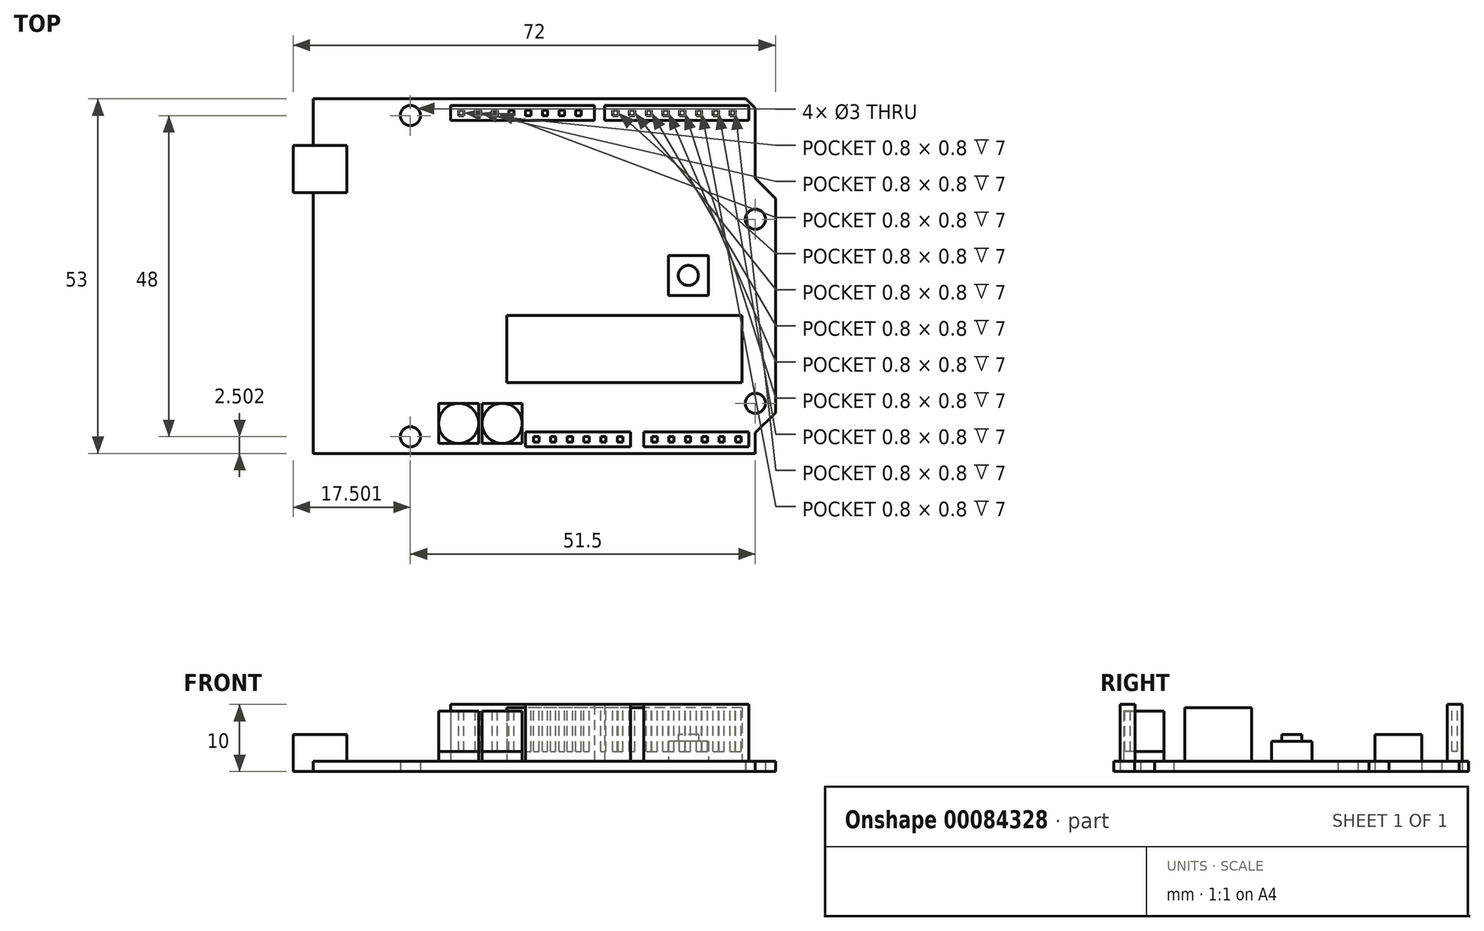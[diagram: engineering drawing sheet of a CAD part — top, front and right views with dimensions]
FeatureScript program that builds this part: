
annotation { "Feature Type Name" : "Feature", "Feature Type Description" : "" }
export const myFeature = defineFeature(function(context is Context, id is Id, definition is map)
    precondition{}
    {
        {
            var Q0;
            Q0=qCreatedBy(makeId("Top.planeOp"),FACE);
            var sketch = newSketch(context, id + "F0", { "sketchPlane" : qUnion([Q0])});
            skLineSegment(sketch, "E0.bottom", {"start": v(-32.88, 24.03) * mm, "end": v(31.7, 24.03) * mm});
            skLineSegment(sketch, "E0.top", {"start": v(-32.88, -28.97) * mm, "end": v(33.12, -28.97) * mm});
            skLineSegment(sketch, "E0.left", {"start": v(-32.88, 24.03) * mm, "end": v(-32.88, -28.97) * mm});
            skLineSegment(sketch, "E0.right", {"start": v(36.12, 9.14) * mm, "end": v(36.12, -22.86) * mm});
            skLineSegment(sketch, "E1", {"start": v(33.12, 22.62) * mm, "end": v(33.12, 12.14) * mm});
            skLineSegment(sketch, "E2", {"start": v(33.12, 12.14) * mm, "end": v(36.12, 9.14) * mm});
            skLineSegment(sketch, "E3", {"start": v(33.12, -25.86) * mm, "end": v(36.12, -22.86) * mm});
            skPoint(sketch, "E4.orphan", {"position": v(36.12, 24.03) * mm});
            skPoint(sketch, "E5.end.orphan", {"position": v(36.12, 11.53) * mm});
            skPoint(sketch, "E6.end.orphan", {"position": v(36.12, -26.47) * mm});
            skPoint(sketch, "E7.orphan", {"position": v(36.12, -28.97) * mm});
            skLineSegment(sketch, "E8.trimOffspring", {"start": v(33.12, -25.86) * mm, "end": v(33.12, -28.97) * mm});
            skCircle(sketch, "E9", {"center": v(33.12, -21.47) * mm, "radius": 1.5 * mm});
            skCircle(sketch, "E10", {"center": v(33.12, 6.03) * mm, "radius": 1.5 * mm});
            skLineSegment(sketch, "E11", {"start": v(31.7, 24.03) * mm, "end": v(33.12, 22.62) * mm});
            skPoint(sketch, "E12.orphan", {"position": v(33.12, 24.03) * mm});
            skCircle(sketch, "E13", {"center": v(-18.38, -26.47) * mm, "radius": 1.5 * mm});
            skCircle(sketch, "E14", {"center": v(-18.38, 21.53) * mm, "radius": 1.5 * mm});
            skLineSegment(sketch, "E15.bottom", {"start": v(-27.88, 17.03) * mm, "end": v(-35.88, 17.03) * mm});
            skLineSegment(sketch, "E15.top", {"start": v(-27.88, 10.03) * mm, "end": v(-35.88, 10.03) * mm});
            skLineSegment(sketch, "E15.left", {"start": v(-27.88, 17.03) * mm, "end": v(-27.88, 10.03) * mm});
            skLineSegment(sketch, "E15.right", {"start": v(-35.88, 17.03) * mm, "end": v(-35.88, 10.03) * mm});
            skSolve(sketch);
        }
        {
            var Q0;
            {var subQ4=sQuery(id+"F0.wireOp",EDGE,"E0.bottom");Q0=makeQuery(id+"F0.imprint","IMPRINT",FACE,{"disambiguationData":[TD([[makeQuery(id+"F0.imprint","IMPRINT",EDGE,{"derivedFrom":subQ4}),-1.0]])]});}
            extrude(context, id + "F1", {"entities" : qUnion([Q0]), "depth" : 1.5 * mm});
        }
        {
            var Q0;
            {var subQ5=sQuery(id+"F0.wireOp",EDGE,"E15.left");Q0=makeQuery(id+"F0.imprint","IMPRINT",FACE,{"disambiguationData":[TD([[makeQuery(id+"F0.imprint","IMPRINT",EDGE,{"derivedFrom":subQ5}),-1.0]])]});}
            var sketch = newSketch(context, id + "F2", { "sketchPlane" : qUnion([Q0])});
            skLineSegment(sketch, "E16.bottom", {"start": v(-27.88, 10.03) * mm, "end": v(-35.88, 10.03) * mm});
            skLineSegment(sketch, "E16.top", {"start": v(-27.88, 17.03) * mm, "end": v(-35.88, 17.03) * mm});
            skLineSegment(sketch, "E16.left", {"start": v(-27.88, 10.03) * mm, "end": v(-27.88, 17.03) * mm});
            skLineSegment(sketch, "E16.right", {"start": v(-35.88, 10.03) * mm, "end": v(-35.88, 17.03) * mm});
            skSolve(sketch);
        }
        {
            var Q0;
            Q0 = qSketchRegion(id + "F2", true);
            extrude(context, id + "F3", {"entities" : qUnion([Q0]), "operationType" : NewBodyOperationType.ADD, "depth" : 5.5 * mm});
        }
        {
            var Q0;
            Q0=makeQuery(id+"F1.opExtrude","CAP_FACE",FACE,{"disambiguationData":[OSD([sQuery(id+"F0.wireOp",EDGE,"E0.bottom"),sQuery(id+"F0.wireOp",EDGE,"E0.top"),sQuery(id+"F0.wireOp",EDGE,"E0.left"),sQuery(id+"F0.wireOp",EDGE,"E0.right"),sQuery(id+"F0.wireOp",EDGE,"E1"),sQuery(id+"F0.wireOp",EDGE,"E2"),sQuery(id+"F0.wireOp",EDGE,"E3"),sQuery(id+"F0.wireOp",EDGE,"E8.trimOffspring"),sQuery(id+"F0.wireOp",EDGE,"E9"),sQuery(id+"F0.wireOp",EDGE,"E10"),sQuery(id+"F0.wireOp",EDGE,"E11"),sQuery(id+"F0.wireOp",EDGE,"E13"),sQuery(id+"F0.wireOp",EDGE,"E14"),sQuery(id+"F0.wireOp",EDGE,"E15.bottom"),sQuery(id+"F0.wireOp",EDGE,"E15.top"),sQuery(id+"F0.wireOp",EDGE,"E15.left")])],"isStart":false});
            var sketch = newSketch(context, id + "F4", { "sketchPlane" : qUnion([Q0])});
            skLineSegment(sketch, "E17.bottom", {"start": v(32.12, 23.03) * mm, "end": v(10.62, 23.03) * mm});
            skLineSegment(sketch, "E17.top", {"start": v(32.12, 20.83) * mm, "end": v(10.62, 20.83) * mm});
            skLineSegment(sketch, "E17.left", {"start": v(32.12, 23.03) * mm, "end": v(32.12, 20.83) * mm});
            skLineSegment(sketch, "E17.right", {"start": v(10.62, 23.03) * mm, "end": v(10.62, 20.83) * mm});
            skLineSegment(sketch, "E18.bottom", {"start": v(9.12, 23.03) * mm, "end": v(-12.38, 23.03) * mm});
            skLineSegment(sketch, "E18.top", {"start": v(9.12, 20.83) * mm, "end": v(-12.38, 20.83) * mm});
            skLineSegment(sketch, "E18.left", {"start": v(9.12, 23.03) * mm, "end": v(9.12, 20.83) * mm});
            skLineSegment(sketch, "E18.right", {"start": v(-12.38, 23.03) * mm, "end": v(-12.38, 20.83) * mm});
            skLineSegment(sketch, "E19.bottom", {"start": v(32.12, -27.97) * mm, "end": v(16.47, -27.97) * mm});
            skLineSegment(sketch, "E19.top", {"start": v(32.12, -25.77) * mm, "end": v(16.47, -25.77) * mm});
            skLineSegment(sketch, "E19.left", {"start": v(32.12, -27.97) * mm, "end": v(32.12, -25.77) * mm});
            skLineSegment(sketch, "E19.right", {"start": v(16.47, -27.97) * mm, "end": v(16.47, -25.77) * mm});
            skLineSegment(sketch, "E20.bottom", {"start": v(14.47, -27.97) * mm, "end": v(-1.18, -27.97) * mm});
            skLineSegment(sketch, "E20.top", {"start": v(14.47, -25.77) * mm, "end": v(-1.18, -25.77) * mm});
            skLineSegment(sketch, "E20.left", {"start": v(14.47, -27.97) * mm, "end": v(14.47, -25.77) * mm});
            skLineSegment(sketch, "E20.right", {"start": v(-1.18, -27.97) * mm, "end": v(-1.18, -25.77) * mm});
            skSolve(sketch);
        }
        {
            var Q0;
            Q0 = qSketchRegion(id + "F4", true);
            extrude(context, id + "F5", {"entities" : qUnion([Q0]), "operationType" : NewBodyOperationType.ADD, "depth" : 8.5 * mm});
        }
        {
            var Q0;
            Q0=makeQuery(id+"F1.opExtrude","CAP_FACE",FACE,{"disambiguationData":[OSD([sQuery(id+"F0.wireOp",EDGE,"E0.bottom"),sQuery(id+"F0.wireOp",EDGE,"E0.top"),sQuery(id+"F0.wireOp",EDGE,"E0.left"),sQuery(id+"F0.wireOp",EDGE,"E0.right"),sQuery(id+"F0.wireOp",EDGE,"E1"),sQuery(id+"F0.wireOp",EDGE,"E2"),sQuery(id+"F0.wireOp",EDGE,"E3"),sQuery(id+"F0.wireOp",EDGE,"E8.trimOffspring"),sQuery(id+"F0.wireOp",EDGE,"E9"),sQuery(id+"F0.wireOp",EDGE,"E10"),sQuery(id+"F0.wireOp",EDGE,"E11"),sQuery(id+"F0.wireOp",EDGE,"E13"),sQuery(id+"F0.wireOp",EDGE,"E14"),sQuery(id+"F0.wireOp",EDGE,"E15.bottom"),sQuery(id+"F0.wireOp",EDGE,"E15.top"),sQuery(id+"F0.wireOp",EDGE,"E15.left")])],"isStart":false});
            var sketch = newSketch(context, id + "F6", { "sketchPlane" : qUnion([Q0])});
            skLineSegment(sketch, "E21.bottom", {"start": v(31.12, -18.37) * mm, "end": v(-3.98, -18.37) * mm});
            skLineSegment(sketch, "E21.top", {"start": v(31.12, -8.37) * mm, "end": v(-3.98, -8.37) * mm});
            skLineSegment(sketch, "E21.left", {"start": v(31.12, -18.37) * mm, "end": v(31.12, -8.37) * mm});
            skLineSegment(sketch, "E21.right", {"start": v(-3.98, -18.37) * mm, "end": v(-3.98, -8.37) * mm});
            skSolve(sketch);
        }
        {
            var Q0;
            Q0 = qSketchRegion(id + "F6", true);
            extrude(context, id + "F7", {"entities" : qUnion([Q0]), "operationType" : NewBodyOperationType.ADD, "depth" : 8 * mm});
        }
        {
            var Q0;
            Q0=makeQuery(id+"F5.opExtrude","CAP_FACE",FACE,{"disambiguationData":[OSD([sQuery(id+"F4.wireOp",EDGE,"E20.bottom"),sQuery(id+"F4.wireOp",EDGE,"E20.top"),sQuery(id+"F4.wireOp",EDGE,"E20.left"),sQuery(id+"F4.wireOp",EDGE,"E20.right")])],"isStart":false});
            var sketch = newSketch(context, id + "F8", { "sketchPlane" : qUnion([Q0])});
            skLineSegment(sketch, "E22.bottom", {"start": v(0.02, -26.47) * mm, "end": v(0.82, -26.47) * mm});
            skLineSegment(sketch, "E22.top", {"start": v(0.02, -27.27) * mm, "end": v(0.82, -27.27) * mm});
            skLineSegment(sketch, "E22.left", {"start": v(0.02, -26.47) * mm, "end": v(0.02, -27.27) * mm});
            skLineSegment(sketch, "E22.right", {"start": v(0.82, -26.47) * mm, "end": v(0.82, -27.27) * mm});
            skLineSegment(sketch, "E23.bottom", {"start": v(-0.48, -25.97) * mm, "end": v(1.32, -25.97) * mm});
            skLineSegment(sketch, "E23.top", {"start": v(-0.48, -27.77) * mm, "end": v(1.32, -27.77) * mm});
            skLineSegment(sketch, "E23.left", {"start": v(-0.48, -25.97) * mm, "end": v(-0.48, -27.77) * mm});
            skLineSegment(sketch, "E23.right", {"start": v(1.32, -25.97) * mm, "end": v(1.32, -27.77) * mm});
            skLineSegment(sketch, "E24.bottom", {"start": v(2.52, -26.47) * mm, "end": v(3.32, -26.47) * mm});
            skLineSegment(sketch, "E24.top", {"start": v(2.52, -27.27) * mm, "end": v(3.32, -27.27) * mm});
            skLineSegment(sketch, "E24.left", {"start": v(2.52, -26.47) * mm, "end": v(2.52, -27.27) * mm});
            skLineSegment(sketch, "E24.right", {"start": v(3.32, -26.47) * mm, "end": v(3.32, -27.27) * mm});
            skLineSegment(sketch, "E25.bottom", {"start": v(2.02, -25.97) * mm, "end": v(3.82, -25.97) * mm});
            skLineSegment(sketch, "E25.top", {"start": v(2.02, -27.77) * mm, "end": v(3.82, -27.77) * mm});
            skLineSegment(sketch, "E25.left", {"start": v(2.02, -25.97) * mm, "end": v(2.02, -27.77) * mm});
            skLineSegment(sketch, "E25.right", {"start": v(3.82, -25.97) * mm, "end": v(3.82, -27.77) * mm});
            skLineSegment(sketch, "E26.bottom", {"start": v(5.02, -26.47) * mm, "end": v(5.82, -26.47) * mm});
            skLineSegment(sketch, "E26.top", {"start": v(5.02, -27.27) * mm, "end": v(5.82, -27.27) * mm});
            skLineSegment(sketch, "E26.left", {"start": v(5.02, -26.47) * mm, "end": v(5.02, -27.27) * mm});
            skLineSegment(sketch, "E26.right", {"start": v(5.82, -26.47) * mm, "end": v(5.82, -27.27) * mm});
            skLineSegment(sketch, "E27.bottom", {"start": v(4.52, -25.97) * mm, "end": v(6.32, -25.97) * mm});
            skLineSegment(sketch, "E27.top", {"start": v(4.52, -27.77) * mm, "end": v(6.32, -27.77) * mm});
            skLineSegment(sketch, "E27.left", {"start": v(4.52, -25.97) * mm, "end": v(4.52, -27.77) * mm});
            skLineSegment(sketch, "E27.right", {"start": v(6.32, -25.97) * mm, "end": v(6.32, -27.77) * mm});
            skLineSegment(sketch, "E28.bottom", {"start": v(7.52, -26.47) * mm, "end": v(8.32, -26.47) * mm});
            skLineSegment(sketch, "E28.top", {"start": v(7.52, -27.27) * mm, "end": v(8.32, -27.27) * mm});
            skLineSegment(sketch, "E28.left", {"start": v(7.52, -26.47) * mm, "end": v(7.52, -27.27) * mm});
            skLineSegment(sketch, "E28.right", {"start": v(8.32, -26.47) * mm, "end": v(8.32, -27.27) * mm});
            skLineSegment(sketch, "E29.bottom", {"start": v(7.02, -25.97) * mm, "end": v(8.82, -25.97) * mm});
            skLineSegment(sketch, "E29.top", {"start": v(7.02, -27.77) * mm, "end": v(8.82, -27.77) * mm});
            skLineSegment(sketch, "E29.left", {"start": v(7.02, -25.97) * mm, "end": v(7.02, -27.77) * mm});
            skLineSegment(sketch, "E29.right", {"start": v(8.82, -25.97) * mm, "end": v(8.82, -27.77) * mm});
            skLineSegment(sketch, "E30.bottom", {"start": v(10.02, -26.47) * mm, "end": v(10.82, -26.47) * mm});
            skLineSegment(sketch, "E30.top", {"start": v(10.02, -27.27) * mm, "end": v(10.82, -27.27) * mm});
            skLineSegment(sketch, "E30.left", {"start": v(10.02, -26.47) * mm, "end": v(10.02, -27.27) * mm});
            skLineSegment(sketch, "E30.right", {"start": v(10.82, -26.47) * mm, "end": v(10.82, -27.27) * mm});
            skLineSegment(sketch, "E31.bottom", {"start": v(9.52, -25.97) * mm, "end": v(11.32, -25.97) * mm});
            skLineSegment(sketch, "E31.top", {"start": v(9.52, -27.77) * mm, "end": v(11.32, -27.77) * mm});
            skLineSegment(sketch, "E31.left", {"start": v(9.52, -25.97) * mm, "end": v(9.52, -27.77) * mm});
            skLineSegment(sketch, "E31.right", {"start": v(11.32, -25.97) * mm, "end": v(11.32, -27.77) * mm});
            skLineSegment(sketch, "E32.bottom", {"start": v(12.52, -26.47) * mm, "end": v(13.32, -26.47) * mm});
            skLineSegment(sketch, "E32.top", {"start": v(12.52, -27.27) * mm, "end": v(13.32, -27.27) * mm});
            skLineSegment(sketch, "E32.left", {"start": v(12.52, -26.47) * mm, "end": v(12.52, -27.27) * mm});
            skLineSegment(sketch, "E32.right", {"start": v(13.32, -26.47) * mm, "end": v(13.32, -27.27) * mm});
            skLineSegment(sketch, "E33.bottom", {"start": v(12.02, -25.97) * mm, "end": v(13.82, -25.97) * mm});
            skLineSegment(sketch, "E33.top", {"start": v(12.02, -27.77) * mm, "end": v(13.82, -27.77) * mm});
            skLineSegment(sketch, "E33.left", {"start": v(12.02, -25.97) * mm, "end": v(12.02, -27.77) * mm});
            skLineSegment(sketch, "E33.right", {"start": v(13.82, -25.97) * mm, "end": v(13.82, -27.77) * mm});
            skLineSegment(sketch, "E34.bottom", {"start": v(17.67, -26.47) * mm, "end": v(18.47, -26.47) * mm});
            skLineSegment(sketch, "E34.top", {"start": v(17.67, -27.27) * mm, "end": v(18.47, -27.27) * mm});
            skLineSegment(sketch, "E34.left", {"start": v(17.67, -26.47) * mm, "end": v(17.67, -27.27) * mm});
            skLineSegment(sketch, "E34.right", {"start": v(18.47, -26.47) * mm, "end": v(18.47, -27.27) * mm});
            skLineSegment(sketch, "E35.bottom", {"start": v(17.17, -25.97) * mm, "end": v(18.97, -25.97) * mm});
            skLineSegment(sketch, "E35.top", {"start": v(17.17, -27.77) * mm, "end": v(18.97, -27.77) * mm});
            skLineSegment(sketch, "E35.left", {"start": v(17.17, -25.97) * mm, "end": v(17.17, -27.77) * mm});
            skLineSegment(sketch, "E35.right", {"start": v(18.97, -25.97) * mm, "end": v(18.97, -27.77) * mm});
            skLineSegment(sketch, "E36.bottom", {"start": v(20.17, -26.47) * mm, "end": v(20.97, -26.47) * mm});
            skLineSegment(sketch, "E36.top", {"start": v(20.17, -27.27) * mm, "end": v(20.97, -27.27) * mm});
            skLineSegment(sketch, "E36.left", {"start": v(20.17, -26.47) * mm, "end": v(20.17, -27.27) * mm});
            skLineSegment(sketch, "E36.right", {"start": v(20.97, -26.47) * mm, "end": v(20.97, -27.27) * mm});
            skLineSegment(sketch, "E37.bottom", {"start": v(19.67, -25.97) * mm, "end": v(21.47, -25.97) * mm});
            skLineSegment(sketch, "E37.top", {"start": v(19.67, -27.77) * mm, "end": v(21.47, -27.77) * mm});
            skLineSegment(sketch, "E37.left", {"start": v(19.67, -25.97) * mm, "end": v(19.67, -27.77) * mm});
            skLineSegment(sketch, "E37.right", {"start": v(21.47, -25.97) * mm, "end": v(21.47, -27.77) * mm});
            skLineSegment(sketch, "E38.bottom", {"start": v(22.67, -26.47) * mm, "end": v(23.47, -26.47) * mm});
            skLineSegment(sketch, "E38.top", {"start": v(22.67, -27.27) * mm, "end": v(23.47, -27.27) * mm});
            skLineSegment(sketch, "E38.left", {"start": v(22.67, -26.47) * mm, "end": v(22.67, -27.27) * mm});
            skLineSegment(sketch, "E38.right", {"start": v(23.47, -26.47) * mm, "end": v(23.47, -27.27) * mm});
            skLineSegment(sketch, "E39.bottom", {"start": v(22.17, -25.97) * mm, "end": v(23.97, -25.97) * mm});
            skLineSegment(sketch, "E39.top", {"start": v(22.17, -27.77) * mm, "end": v(23.97, -27.77) * mm});
            skLineSegment(sketch, "E39.left", {"start": v(22.17, -25.97) * mm, "end": v(22.17, -27.77) * mm});
            skLineSegment(sketch, "E39.right", {"start": v(23.97, -25.97) * mm, "end": v(23.97, -27.77) * mm});
            skLineSegment(sketch, "E40.bottom", {"start": v(25.17, -26.47) * mm, "end": v(25.97, -26.47) * mm});
            skLineSegment(sketch, "E40.top", {"start": v(25.17, -27.27) * mm, "end": v(25.97, -27.27) * mm});
            skLineSegment(sketch, "E40.left", {"start": v(25.17, -26.47) * mm, "end": v(25.17, -27.27) * mm});
            skLineSegment(sketch, "E40.right", {"start": v(25.97, -26.47) * mm, "end": v(25.97, -27.27) * mm});
            skLineSegment(sketch, "E41.bottom", {"start": v(24.67, -25.97) * mm, "end": v(26.47, -25.97) * mm});
            skLineSegment(sketch, "E41.top", {"start": v(24.67, -27.77) * mm, "end": v(26.47, -27.77) * mm});
            skLineSegment(sketch, "E41.left", {"start": v(24.67, -25.97) * mm, "end": v(24.67, -27.77) * mm});
            skLineSegment(sketch, "E41.right", {"start": v(26.47, -25.97) * mm, "end": v(26.47, -27.77) * mm});
            skLineSegment(sketch, "E42.bottom", {"start": v(27.67, -26.47) * mm, "end": v(28.47, -26.47) * mm});
            skLineSegment(sketch, "E42.top", {"start": v(27.67, -27.27) * mm, "end": v(28.47, -27.27) * mm});
            skLineSegment(sketch, "E42.left", {"start": v(27.67, -26.47) * mm, "end": v(27.67, -27.27) * mm});
            skLineSegment(sketch, "E42.right", {"start": v(28.47, -26.47) * mm, "end": v(28.47, -27.27) * mm});
            skLineSegment(sketch, "E43.bottom", {"start": v(27.17, -25.97) * mm, "end": v(28.97, -25.97) * mm});
            skLineSegment(sketch, "E43.top", {"start": v(27.17, -27.77) * mm, "end": v(28.97, -27.77) * mm});
            skLineSegment(sketch, "E43.left", {"start": v(27.17, -25.97) * mm, "end": v(27.17, -27.77) * mm});
            skLineSegment(sketch, "E43.right", {"start": v(28.97, -25.97) * mm, "end": v(28.97, -27.77) * mm});
            skLineSegment(sketch, "E44.bottom", {"start": v(30.17, -26.47) * mm, "end": v(30.97, -26.47) * mm});
            skLineSegment(sketch, "E44.top", {"start": v(30.17, -27.27) * mm, "end": v(30.97, -27.27) * mm});
            skLineSegment(sketch, "E44.left", {"start": v(30.17, -26.47) * mm, "end": v(30.17, -27.27) * mm});
            skLineSegment(sketch, "E44.right", {"start": v(30.97, -26.47) * mm, "end": v(30.97, -27.27) * mm});
            skLineSegment(sketch, "E45.bottom", {"start": v(29.67, -25.97) * mm, "end": v(31.47, -25.97) * mm});
            skLineSegment(sketch, "E45.top", {"start": v(29.67, -27.77) * mm, "end": v(31.47, -27.77) * mm});
            skLineSegment(sketch, "E45.left", {"start": v(29.67, -25.97) * mm, "end": v(29.67, -27.77) * mm});
            skLineSegment(sketch, "E45.right", {"start": v(31.47, -25.97) * mm, "end": v(31.47, -27.77) * mm});
            skLineSegment(sketch, "E46.bottom", {"start": v(-11.18, 22.33) * mm, "end": v(-10.38, 22.33) * mm});
            skLineSegment(sketch, "E46.top", {"start": v(-11.18, 21.53) * mm, "end": v(-10.38, 21.53) * mm});
            skLineSegment(sketch, "E46.left", {"start": v(-11.18, 22.33) * mm, "end": v(-11.18, 21.53) * mm});
            skLineSegment(sketch, "E46.right", {"start": v(-10.38, 22.33) * mm, "end": v(-10.38, 21.53) * mm});
            skLineSegment(sketch, "E47.bottom", {"start": v(-11.68, 22.83) * mm, "end": v(-9.88, 22.83) * mm});
            skLineSegment(sketch, "E47.top", {"start": v(-11.68, 21.03) * mm, "end": v(-9.88, 21.03) * mm});
            skLineSegment(sketch, "E47.left", {"start": v(-11.68, 22.83) * mm, "end": v(-11.68, 21.03) * mm});
            skLineSegment(sketch, "E47.right", {"start": v(-9.88, 22.83) * mm, "end": v(-9.88, 21.03) * mm});
            skLineSegment(sketch, "E48.bottom", {"start": v(-8.68, 22.33) * mm, "end": v(-7.88, 22.33) * mm});
            skLineSegment(sketch, "E48.top", {"start": v(-8.68, 21.53) * mm, "end": v(-7.88, 21.53) * mm});
            skLineSegment(sketch, "E48.left", {"start": v(-8.68, 22.33) * mm, "end": v(-8.68, 21.53) * mm});
            skLineSegment(sketch, "E48.right", {"start": v(-7.88, 22.33) * mm, "end": v(-7.88, 21.53) * mm});
            skLineSegment(sketch, "E49.bottom", {"start": v(-9.18, 22.83) * mm, "end": v(-7.38, 22.83) * mm});
            skLineSegment(sketch, "E49.top", {"start": v(-9.18, 21.03) * mm, "end": v(-7.38, 21.03) * mm});
            skLineSegment(sketch, "E49.left", {"start": v(-9.18, 22.83) * mm, "end": v(-9.18, 21.03) * mm});
            skLineSegment(sketch, "E49.right", {"start": v(-7.38, 22.83) * mm, "end": v(-7.38, 21.03) * mm});
            skLineSegment(sketch, "E50.bottom", {"start": v(-6.18, 22.33) * mm, "end": v(-5.38, 22.33) * mm});
            skLineSegment(sketch, "E50.top", {"start": v(-6.18, 21.53) * mm, "end": v(-5.38, 21.53) * mm});
            skLineSegment(sketch, "E50.left", {"start": v(-6.18, 22.33) * mm, "end": v(-6.18, 21.53) * mm});
            skLineSegment(sketch, "E50.right", {"start": v(-5.38, 22.33) * mm, "end": v(-5.38, 21.53) * mm});
            skLineSegment(sketch, "E51.bottom", {"start": v(-6.68, 22.83) * mm, "end": v(-4.88, 22.83) * mm});
            skLineSegment(sketch, "E51.top", {"start": v(-6.68, 21.03) * mm, "end": v(-4.88, 21.03) * mm});
            skLineSegment(sketch, "E51.left", {"start": v(-6.68, 22.83) * mm, "end": v(-6.68, 21.03) * mm});
            skLineSegment(sketch, "E51.right", {"start": v(-4.88, 22.83) * mm, "end": v(-4.88, 21.03) * mm});
            skLineSegment(sketch, "E52.bottom", {"start": v(-3.68, 22.33) * mm, "end": v(-2.88, 22.33) * mm});
            skLineSegment(sketch, "E52.top", {"start": v(-3.68, 21.53) * mm, "end": v(-2.88, 21.53) * mm});
            skLineSegment(sketch, "E52.left", {"start": v(-3.68, 22.33) * mm, "end": v(-3.68, 21.53) * mm});
            skLineSegment(sketch, "E52.right", {"start": v(-2.88, 22.33) * mm, "end": v(-2.88, 21.53) * mm});
            skLineSegment(sketch, "E53.bottom", {"start": v(-4.18, 22.83) * mm, "end": v(-2.38, 22.83) * mm});
            skLineSegment(sketch, "E53.top", {"start": v(-4.18, 21.03) * mm, "end": v(-2.38, 21.03) * mm});
            skLineSegment(sketch, "E53.left", {"start": v(-4.18, 22.83) * mm, "end": v(-4.18, 21.03) * mm});
            skLineSegment(sketch, "E53.right", {"start": v(-2.38, 22.83) * mm, "end": v(-2.38, 21.03) * mm});
            skLineSegment(sketch, "E54.bottom", {"start": v(-1.18, 22.33) * mm, "end": v(-0.38, 22.33) * mm});
            skLineSegment(sketch, "E54.top", {"start": v(-1.18, 21.53) * mm, "end": v(-0.38, 21.53) * mm});
            skLineSegment(sketch, "E54.left", {"start": v(-1.18, 22.33) * mm, "end": v(-1.18, 21.53) * mm});
            skLineSegment(sketch, "E54.right", {"start": v(-0.38, 22.33) * mm, "end": v(-0.38, 21.53) * mm});
            skLineSegment(sketch, "E55.bottom", {"start": v(-1.68, 22.83) * mm, "end": v(0.12, 22.83) * mm});
            skLineSegment(sketch, "E55.top", {"start": v(-1.68, 21.03) * mm, "end": v(0.12, 21.03) * mm});
            skLineSegment(sketch, "E55.left", {"start": v(-1.68, 22.83) * mm, "end": v(-1.68, 21.03) * mm});
            skLineSegment(sketch, "E55.right", {"start": v(0.12, 22.83) * mm, "end": v(0.12, 21.03) * mm});
            skLineSegment(sketch, "E56.bottom", {"start": v(1.32, 22.33) * mm, "end": v(2.12, 22.33) * mm});
            skLineSegment(sketch, "E56.top", {"start": v(1.32, 21.53) * mm, "end": v(2.12, 21.53) * mm});
            skLineSegment(sketch, "E56.left", {"start": v(1.32, 22.33) * mm, "end": v(1.32, 21.53) * mm});
            skLineSegment(sketch, "E56.right", {"start": v(2.12, 22.33) * mm, "end": v(2.12, 21.53) * mm});
            skLineSegment(sketch, "E57.bottom", {"start": v(0.82, 22.83) * mm, "end": v(2.62, 22.83) * mm});
            skLineSegment(sketch, "E57.top", {"start": v(0.82, 21.03) * mm, "end": v(2.62, 21.03) * mm});
            skLineSegment(sketch, "E57.left", {"start": v(0.82, 22.83) * mm, "end": v(0.82, 21.03) * mm});
            skLineSegment(sketch, "E57.right", {"start": v(2.62, 22.83) * mm, "end": v(2.62, 21.03) * mm});
            skLineSegment(sketch, "E58.bottom", {"start": v(3.82, 22.33) * mm, "end": v(4.62, 22.33) * mm});
            skLineSegment(sketch, "E58.top", {"start": v(3.82, 21.53) * mm, "end": v(4.62, 21.53) * mm});
            skLineSegment(sketch, "E58.left", {"start": v(3.82, 22.33) * mm, "end": v(3.82, 21.53) * mm});
            skLineSegment(sketch, "E58.right", {"start": v(4.62, 22.33) * mm, "end": v(4.62, 21.53) * mm});
            skLineSegment(sketch, "E59.bottom", {"start": v(3.32, 22.83) * mm, "end": v(5.12, 22.83) * mm});
            skLineSegment(sketch, "E59.top", {"start": v(3.32, 21.03) * mm, "end": v(5.12, 21.03) * mm});
            skLineSegment(sketch, "E59.left", {"start": v(3.32, 22.83) * mm, "end": v(3.32, 21.03) * mm});
            skLineSegment(sketch, "E59.right", {"start": v(5.12, 22.83) * mm, "end": v(5.12, 21.03) * mm});
            skLineSegment(sketch, "E60.bottom", {"start": v(6.32, 22.33) * mm, "end": v(7.12, 22.33) * mm});
            skLineSegment(sketch, "E60.top", {"start": v(6.32, 21.53) * mm, "end": v(7.12, 21.53) * mm});
            skLineSegment(sketch, "E60.left", {"start": v(6.32, 22.33) * mm, "end": v(6.32, 21.53) * mm});
            skLineSegment(sketch, "E60.right", {"start": v(7.12, 22.33) * mm, "end": v(7.12, 21.53) * mm});
            skLineSegment(sketch, "E61.bottom", {"start": v(5.82, 22.83) * mm, "end": v(7.62, 22.83) * mm});
            skLineSegment(sketch, "E61.top", {"start": v(5.82, 21.03) * mm, "end": v(7.62, 21.03) * mm});
            skLineSegment(sketch, "E61.left", {"start": v(5.82, 22.83) * mm, "end": v(5.82, 21.03) * mm});
            skLineSegment(sketch, "E61.right", {"start": v(7.62, 22.83) * mm, "end": v(7.62, 21.03) * mm});
            skLineSegment(sketch, "E62.bottom", {"start": v(11.82, 22.33) * mm, "end": v(12.62, 22.33) * mm});
            skLineSegment(sketch, "E62.top", {"start": v(11.82, 21.53) * mm, "end": v(12.62, 21.53) * mm});
            skLineSegment(sketch, "E62.left", {"start": v(11.82, 22.33) * mm, "end": v(11.82, 21.53) * mm});
            skLineSegment(sketch, "E62.right", {"start": v(12.62, 22.33) * mm, "end": v(12.62, 21.53) * mm});
            skLineSegment(sketch, "E63.bottom", {"start": v(11.32, 22.83) * mm, "end": v(13.12, 22.83) * mm});
            skLineSegment(sketch, "E63.top", {"start": v(11.32, 21.03) * mm, "end": v(13.12, 21.03) * mm});
            skLineSegment(sketch, "E63.left", {"start": v(11.32, 22.83) * mm, "end": v(11.32, 21.03) * mm});
            skLineSegment(sketch, "E63.right", {"start": v(13.12, 22.83) * mm, "end": v(13.12, 21.03) * mm});
            skLineSegment(sketch, "E64.bottom", {"start": v(14.32, 22.33) * mm, "end": v(15.12, 22.33) * mm});
            skLineSegment(sketch, "E64.top", {"start": v(14.32, 21.53) * mm, "end": v(15.12, 21.53) * mm});
            skLineSegment(sketch, "E64.left", {"start": v(14.32, 22.33) * mm, "end": v(14.32, 21.53) * mm});
            skLineSegment(sketch, "E64.right", {"start": v(15.12, 22.33) * mm, "end": v(15.12, 21.53) * mm});
            skLineSegment(sketch, "E65.bottom", {"start": v(13.82, 22.83) * mm, "end": v(15.62, 22.83) * mm});
            skLineSegment(sketch, "E65.top", {"start": v(13.82, 21.03) * mm, "end": v(15.62, 21.03) * mm});
            skLineSegment(sketch, "E65.left", {"start": v(13.82, 22.83) * mm, "end": v(13.82, 21.03) * mm});
            skLineSegment(sketch, "E65.right", {"start": v(15.62, 22.83) * mm, "end": v(15.62, 21.03) * mm});
            skLineSegment(sketch, "E66.bottom", {"start": v(16.82, 22.33) * mm, "end": v(17.62, 22.33) * mm});
            skLineSegment(sketch, "E66.top", {"start": v(16.82, 21.53) * mm, "end": v(17.62, 21.53) * mm});
            skLineSegment(sketch, "E66.left", {"start": v(16.82, 22.33) * mm, "end": v(16.82, 21.53) * mm});
            skLineSegment(sketch, "E66.right", {"start": v(17.62, 22.33) * mm, "end": v(17.62, 21.53) * mm});
            skLineSegment(sketch, "E67.bottom", {"start": v(16.32, 22.83) * mm, "end": v(18.12, 22.83) * mm});
            skLineSegment(sketch, "E67.top", {"start": v(16.32, 21.03) * mm, "end": v(18.12, 21.03) * mm});
            skLineSegment(sketch, "E67.left", {"start": v(16.32, 22.83) * mm, "end": v(16.32, 21.03) * mm});
            skLineSegment(sketch, "E67.right", {"start": v(18.12, 22.83) * mm, "end": v(18.12, 21.03) * mm});
            skLineSegment(sketch, "E68.bottom", {"start": v(19.32, 22.33) * mm, "end": v(20.12, 22.33) * mm});
            skLineSegment(sketch, "E68.top", {"start": v(19.32, 21.53) * mm, "end": v(20.12, 21.53) * mm});
            skLineSegment(sketch, "E68.left", {"start": v(19.32, 22.33) * mm, "end": v(19.32, 21.53) * mm});
            skLineSegment(sketch, "E68.right", {"start": v(20.12, 22.33) * mm, "end": v(20.12, 21.53) * mm});
            skLineSegment(sketch, "E69.bottom", {"start": v(18.82, 22.83) * mm, "end": v(20.62, 22.83) * mm});
            skLineSegment(sketch, "E69.top", {"start": v(18.82, 21.03) * mm, "end": v(20.62, 21.03) * mm});
            skLineSegment(sketch, "E69.left", {"start": v(18.82, 22.83) * mm, "end": v(18.82, 21.03) * mm});
            skLineSegment(sketch, "E69.right", {"start": v(20.62, 22.83) * mm, "end": v(20.62, 21.03) * mm});
            skLineSegment(sketch, "E70.bottom", {"start": v(21.82, 22.33) * mm, "end": v(22.62, 22.33) * mm});
            skLineSegment(sketch, "E70.top", {"start": v(21.82, 21.53) * mm, "end": v(22.62, 21.53) * mm});
            skLineSegment(sketch, "E70.left", {"start": v(21.82, 22.33) * mm, "end": v(21.82, 21.53) * mm});
            skLineSegment(sketch, "E70.right", {"start": v(22.62, 22.33) * mm, "end": v(22.62, 21.53) * mm});
            skLineSegment(sketch, "E71.bottom", {"start": v(21.32, 22.83) * mm, "end": v(23.12, 22.83) * mm});
            skLineSegment(sketch, "E71.top", {"start": v(21.32, 21.03) * mm, "end": v(23.12, 21.03) * mm});
            skLineSegment(sketch, "E71.left", {"start": v(21.32, 22.83) * mm, "end": v(21.32, 21.03) * mm});
            skLineSegment(sketch, "E71.right", {"start": v(23.12, 22.83) * mm, "end": v(23.12, 21.03) * mm});
            skLineSegment(sketch, "E72.bottom", {"start": v(24.32, 22.33) * mm, "end": v(25.12, 22.33) * mm});
            skLineSegment(sketch, "E72.top", {"start": v(24.32, 21.53) * mm, "end": v(25.12, 21.53) * mm});
            skLineSegment(sketch, "E72.left", {"start": v(24.32, 22.33) * mm, "end": v(24.32, 21.53) * mm});
            skLineSegment(sketch, "E72.right", {"start": v(25.12, 22.33) * mm, "end": v(25.12, 21.53) * mm});
            skLineSegment(sketch, "E73.bottom", {"start": v(23.82, 22.83) * mm, "end": v(25.62, 22.83) * mm});
            skLineSegment(sketch, "E73.top", {"start": v(23.82, 21.03) * mm, "end": v(25.62, 21.03) * mm});
            skLineSegment(sketch, "E73.left", {"start": v(23.82, 22.83) * mm, "end": v(23.82, 21.03) * mm});
            skLineSegment(sketch, "E73.right", {"start": v(25.62, 22.83) * mm, "end": v(25.62, 21.03) * mm});
            skLineSegment(sketch, "E74.bottom", {"start": v(26.82, 22.33) * mm, "end": v(27.62, 22.33) * mm});
            skLineSegment(sketch, "E74.top", {"start": v(26.82, 21.53) * mm, "end": v(27.62, 21.53) * mm});
            skLineSegment(sketch, "E74.left", {"start": v(26.82, 22.33) * mm, "end": v(26.82, 21.53) * mm});
            skLineSegment(sketch, "E74.right", {"start": v(27.62, 22.33) * mm, "end": v(27.62, 21.53) * mm});
            skLineSegment(sketch, "E75.bottom", {"start": v(26.32, 22.83) * mm, "end": v(28.12, 22.83) * mm});
            skLineSegment(sketch, "E75.top", {"start": v(26.32, 21.03) * mm, "end": v(28.12, 21.03) * mm});
            skLineSegment(sketch, "E75.left", {"start": v(26.32, 22.83) * mm, "end": v(26.32, 21.03) * mm});
            skLineSegment(sketch, "E75.right", {"start": v(28.12, 22.83) * mm, "end": v(28.12, 21.03) * mm});
            skLineSegment(sketch, "E76.bottom", {"start": v(29.32, 22.33) * mm, "end": v(30.12, 22.33) * mm});
            skLineSegment(sketch, "E76.top", {"start": v(29.32, 21.53) * mm, "end": v(30.12, 21.53) * mm});
            skLineSegment(sketch, "E76.left", {"start": v(29.32, 22.33) * mm, "end": v(29.32, 21.53) * mm});
            skLineSegment(sketch, "E76.right", {"start": v(30.12, 22.33) * mm, "end": v(30.12, 21.53) * mm});
            skLineSegment(sketch, "E77.bottom", {"start": v(28.82, 22.83) * mm, "end": v(30.62, 22.83) * mm});
            skLineSegment(sketch, "E77.top", {"start": v(28.82, 21.03) * mm, "end": v(30.62, 21.03) * mm});
            skLineSegment(sketch, "E77.left", {"start": v(28.82, 22.83) * mm, "end": v(28.82, 21.03) * mm});
            skLineSegment(sketch, "E77.right", {"start": v(30.62, 22.83) * mm, "end": v(30.62, 21.03) * mm});
            skSolve(sketch);
        }
        {
            var Q0;
            Q0=makeQuery(id+"F8.imprint","IMPRINT",FACE,{"disambiguationData":[TD([[makeQuery(id+"F8.imprint","IMPRINT",EDGE,{"derivedFrom":sQuery(id+"F8.wireOp",EDGE,"E60.bottom")}),-1.0]])]});
            var Q1;
            Q1=makeQuery(id+"F8.imprint","IMPRINT",FACE,{"disambiguationData":[TD([[makeQuery(id+"F8.imprint","IMPRINT",EDGE,{"derivedFrom":sQuery(id+"F8.wireOp",EDGE,"E58.bottom")}),-1.0]])]});
            var Q2;
            Q2=makeQuery(id+"F8.imprint","IMPRINT",FACE,{"disambiguationData":[TD([[makeQuery(id+"F8.imprint","IMPRINT",EDGE,{"derivedFrom":sQuery(id+"F8.wireOp",EDGE,"E62.bottom")}),-1.0]])]});
            var Q3;
            Q3=makeQuery(id+"F8.imprint","IMPRINT",FACE,{"disambiguationData":[TD([[makeQuery(id+"F8.imprint","IMPRINT",EDGE,{"derivedFrom":sQuery(id+"F8.wireOp",EDGE,"E64.bottom")}),-1.0]])]});
            var Q4;
            Q4=makeQuery(id+"F8.imprint","IMPRINT",FACE,{"disambiguationData":[TD([[makeQuery(id+"F8.imprint","IMPRINT",EDGE,{"derivedFrom":sQuery(id+"F8.wireOp",EDGE,"E66.bottom")}),-1.0]])]});
            var Q5;
            Q5=makeQuery(id+"F8.imprint","IMPRINT",FACE,{"disambiguationData":[TD([[makeQuery(id+"F8.imprint","IMPRINT",EDGE,{"derivedFrom":sQuery(id+"F8.wireOp",EDGE,"E68.bottom")}),-1.0]])]});
            var Q6;
            Q6=makeQuery(id+"F8.imprint","IMPRINT",FACE,{"disambiguationData":[TD([[makeQuery(id+"F8.imprint","IMPRINT",EDGE,{"derivedFrom":sQuery(id+"F8.wireOp",EDGE,"E70.bottom")}),-1.0]])]});
            var Q7;
            Q7=makeQuery(id+"F8.imprint","IMPRINT",FACE,{"disambiguationData":[TD([[makeQuery(id+"F8.imprint","IMPRINT",EDGE,{"derivedFrom":sQuery(id+"F8.wireOp",EDGE,"E74.bottom")}),-1.0]])]});
            var Q8;
            Q8=makeQuery(id+"F8.imprint","IMPRINT",FACE,{"disambiguationData":[TD([[makeQuery(id+"F8.imprint","IMPRINT",EDGE,{"derivedFrom":sQuery(id+"F8.wireOp",EDGE,"E76.bottom")}),-1.0]])]});
            var Q9;
            Q9=makeQuery(id+"F8.imprint","IMPRINT",FACE,{"disambiguationData":[TD([[makeQuery(id+"F8.imprint","IMPRINT",EDGE,{"derivedFrom":sQuery(id+"F8.wireOp",EDGE,"E72.bottom")}),-1.0]])]});
            var Q10;
            Q10=makeQuery(id+"F8.imprint","IMPRINT",FACE,{"disambiguationData":[TD([[makeQuery(id+"F8.imprint","IMPRINT",EDGE,{"derivedFrom":sQuery(id+"F8.wireOp",EDGE,"E46.bottom")}),-1.0]])]});
            var Q11;
            Q11=makeQuery(id+"F8.imprint","IMPRINT",FACE,{"disambiguationData":[TD([[makeQuery(id+"F8.imprint","IMPRINT",EDGE,{"derivedFrom":sQuery(id+"F8.wireOp",EDGE,"E48.bottom")}),-1.0]])]});
            var Q12;
            Q12=makeQuery(id+"F8.imprint","IMPRINT",FACE,{"disambiguationData":[TD([[makeQuery(id+"F8.imprint","IMPRINT",EDGE,{"derivedFrom":sQuery(id+"F8.wireOp",EDGE,"E50.bottom")}),-1.0]])]});
            var Q13;
            Q13=makeQuery(id+"F8.imprint","IMPRINT",FACE,{"disambiguationData":[TD([[makeQuery(id+"F8.imprint","IMPRINT",EDGE,{"derivedFrom":sQuery(id+"F8.wireOp",EDGE,"E52.bottom")}),-1.0]])]});
            var Q14;
            Q14=makeQuery(id+"F8.imprint","IMPRINT",FACE,{"disambiguationData":[TD([[makeQuery(id+"F8.imprint","IMPRINT",EDGE,{"derivedFrom":sQuery(id+"F8.wireOp",EDGE,"E54.bottom")}),-1.0]])]});
            var Q15;
            Q15=makeQuery(id+"F8.imprint","IMPRINT",FACE,{"disambiguationData":[TD([[makeQuery(id+"F8.imprint","IMPRINT",EDGE,{"derivedFrom":sQuery(id+"F8.wireOp",EDGE,"E56.bottom")}),-1.0]])]});
            var Q16;
            Q16=makeQuery(id+"F8.imprint","IMPRINT",FACE,{"disambiguationData":[TD([[makeQuery(id+"F8.imprint","IMPRINT",EDGE,{"derivedFrom":sQuery(id+"F8.wireOp",EDGE,"E22.bottom")}),-1.0]])]});
            var Q17;
            Q17=makeQuery(id+"F8.imprint","IMPRINT",FACE,{"disambiguationData":[TD([[makeQuery(id+"F8.imprint","IMPRINT",EDGE,{"derivedFrom":sQuery(id+"F8.wireOp",EDGE,"E24.bottom")}),-1.0]])]});
            var Q18;
            Q18=makeQuery(id+"F8.imprint","IMPRINT",FACE,{"disambiguationData":[TD([[makeQuery(id+"F8.imprint","IMPRINT",EDGE,{"derivedFrom":sQuery(id+"F8.wireOp",EDGE,"E28.bottom")}),-1.0]])]});
            var Q19;
            Q19=makeQuery(id+"F8.imprint","IMPRINT",FACE,{"disambiguationData":[TD([[makeQuery(id+"F8.imprint","IMPRINT",EDGE,{"derivedFrom":sQuery(id+"F8.wireOp",EDGE,"E30.bottom")}),-1.0]])]});
            var Q20;
            Q20=makeQuery(id+"F8.imprint","IMPRINT",FACE,{"disambiguationData":[TD([[makeQuery(id+"F8.imprint","IMPRINT",EDGE,{"derivedFrom":sQuery(id+"F8.wireOp",EDGE,"E32.bottom")}),-1.0]])]});
            var Q21;
            Q21=makeQuery(id+"F8.imprint","IMPRINT",FACE,{"disambiguationData":[TD([[makeQuery(id+"F8.imprint","IMPRINT",EDGE,{"derivedFrom":sQuery(id+"F8.wireOp",EDGE,"E34.bottom")}),-1.0]])]});
            var Q22;
            Q22=makeQuery(id+"F8.imprint","IMPRINT",FACE,{"disambiguationData":[TD([[makeQuery(id+"F8.imprint","IMPRINT",EDGE,{"derivedFrom":sQuery(id+"F8.wireOp",EDGE,"E36.bottom")}),-1.0]])]});
            var Q23;
            Q23=makeQuery(id+"F8.imprint","IMPRINT",FACE,{"disambiguationData":[TD([[makeQuery(id+"F8.imprint","IMPRINT",EDGE,{"derivedFrom":sQuery(id+"F8.wireOp",EDGE,"E38.bottom")}),-1.0]])]});
            var Q24;
            Q24=makeQuery(id+"F8.imprint","IMPRINT",FACE,{"disambiguationData":[TD([[makeQuery(id+"F8.imprint","IMPRINT",EDGE,{"derivedFrom":sQuery(id+"F8.wireOp",EDGE,"E40.bottom")}),-1.0]])]});
            var Q25;
            Q25=makeQuery(id+"F8.imprint","IMPRINT",FACE,{"disambiguationData":[TD([[makeQuery(id+"F8.imprint","IMPRINT",EDGE,{"derivedFrom":sQuery(id+"F8.wireOp",EDGE,"E42.bottom")}),-1.0]])]});
            var Q26;
            Q26=makeQuery(id+"F8.imprint","IMPRINT",FACE,{"disambiguationData":[TD([[makeQuery(id+"F8.imprint","IMPRINT",EDGE,{"derivedFrom":sQuery(id+"F8.wireOp",EDGE,"E44.bottom")}),-1.0]])]});
            var Q27;
            Q27=makeQuery(id+"F8.imprint","IMPRINT",FACE,{"disambiguationData":[TD([[makeQuery(id+"F8.imprint","IMPRINT",EDGE,{"derivedFrom":sQuery(id+"F8.wireOp",EDGE,"E26.bottom")}),-1.0]])]});
            extrude(context, id + "F9", {"entities" : qUnion([Q0, Q1, Q2, Q3, Q4, Q5, Q6, Q7, Q8, Q9, Q10, Q11, Q12, Q13, Q14, Q15, Q16, Q17, Q18, Q19, Q20, Q21, Q22, Q23, Q24, Q25, Q26, Q27]), "operationType" : NewBodyOperationType.REMOVE, "oppositeDirection" : true, "depth" : 7 * mm});
        }
        {
            var Q0;
            Q0=makeQuery(id+"F4.imprint","IMPRINT",FACE,{"disambiguationData":[TD([[makeQuery(id+"F4.imprint","IMPRINT",EDGE,{"derivedFrom":sQuery(id+"F4.wireOp",EDGE,"E17.bottom")}),-1.0]])]});
            var sketch = newSketch(context, id + "F10", { "sketchPlane" : qUnion([Q0])});
            skLineSegment(sketch, "E78.bottom", {"start": v(26.12, -5.37) * mm, "end": v(20.12, -5.37) * mm});
            skLineSegment(sketch, "E78.top", {"start": v(26.12, 0.63) * mm, "end": v(20.12, 0.63) * mm});
            skLineSegment(sketch, "E78.left", {"start": v(26.12, -5.37) * mm, "end": v(26.12, 0.63) * mm});
            skLineSegment(sketch, "E78.right", {"start": v(20.12, -5.37) * mm, "end": v(20.12, 0.63) * mm});
            skSolve(sketch);
        }
        {
            var Q0;
            Q0 = qSketchRegion(id + "F10", true);
            extrude(context, id + "F11", {"entities" : qUnion([Q0]), "operationType" : NewBodyOperationType.ADD, "depth" : 3 * mm});
        }
        {
            var Q0;
            Q0=makeQuery(id+"F11.opExtrude","CAP_FACE",FACE,{"disambiguationData":[OSD([sQuery(id+"F10.wireOp",EDGE,"E78.bottom"),sQuery(id+"F10.wireOp",EDGE,"E78.top"),sQuery(id+"F10.wireOp",EDGE,"E78.left"),sQuery(id+"F10.wireOp",EDGE,"E78.right")])],"isStart":false});
            var sketch = newSketch(context, id + "F12", { "sketchPlane" : qUnion([Q0])});
            skCircle(sketch, "E79", {"center": v(23.12, -2.37) * mm, "radius": 1.5 * mm});
            skPoint(sketch, "E79.centerSnap0", {"position": v(23.12, -5.37) * mm});
            skPoint(sketch, "E79.centerSnap1", {"position": v(20.12, -2.37) * mm});
            skSolve(sketch);
        }
        {
            var Q0;
            Q0 = qSketchRegion(id + "F12", true);
            extrude(context, id + "F13", {"entities" : qUnion([Q0]), "operationType" : NewBodyOperationType.ADD, "depth" : 1 * mm});
        }
        {
            var Q0;
            Q0=makeQuery(id+"F4.imprint","IMPRINT",FACE,{"disambiguationData":[TD([[makeQuery(id+"F4.imprint","IMPRINT",EDGE,{"derivedFrom":sQuery(id+"F4.wireOp",EDGE,"E17.bottom")}),-1.0]])]});
            var sketch = newSketch(context, id + "F14", { "sketchPlane" : qUnion([Q0])});
            skLineSegment(sketch, "E80.bottom", {"start": v(-1.68, -21.47) * mm, "end": v(-7.68, -21.47) * mm});
            skLineSegment(sketch, "E80.top", {"start": v(-1.68, -27.47) * mm, "end": v(-7.68, -27.47) * mm});
            skLineSegment(sketch, "E80.left", {"start": v(-1.68, -21.47) * mm, "end": v(-1.68, -27.47) * mm});
            skLineSegment(sketch, "E80.right", {"start": v(-7.68, -21.47) * mm, "end": v(-7.68, -27.47) * mm});
            skLineSegment(sketch, "E81.bottom", {"start": v(-8.18, -21.47) * mm, "end": v(-14.18, -21.47) * mm});
            skLineSegment(sketch, "E81.top", {"start": v(-8.18, -27.47) * mm, "end": v(-14.18, -27.47) * mm});
            skLineSegment(sketch, "E81.left", {"start": v(-8.18, -21.47) * mm, "end": v(-8.18, -27.47) * mm});
            skLineSegment(sketch, "E81.right", {"start": v(-14.18, -21.47) * mm, "end": v(-14.18, -27.47) * mm});
            skSolve(sketch);
        }
        {
            var Q0;
            Q0 = qSketchRegion(id + "F14", true);
            extrude(context, id + "F15", {"entities" : qUnion([Q0]), "operationType" : NewBodyOperationType.ADD, "depth" : 1.5 * mm});
        }
        {
            var Q0;
            Q0=makeQuery(id+"F15.opExtrude","CAP_FACE",FACE,{"disambiguationData":[OSD([sQuery(id+"F14.wireOp",EDGE,"E81.bottom"),sQuery(id+"F14.wireOp",EDGE,"E81.top"),sQuery(id+"F14.wireOp",EDGE,"E81.left"),sQuery(id+"F14.wireOp",EDGE,"E81.right")])],"isStart":false});
            var sketch = newSketch(context, id + "F16", { "sketchPlane" : qUnion([Q0])});
            skCircle(sketch, "E82", {"center": v(-11.18, -24.47) * mm, "radius": 3 * mm});
            skPoint(sketch, "E82.centerSnap0", {"position": v(-8.18, -24.47) * mm});
            skPoint(sketch, "E82.centerSnap1", {"position": v(-11.18, -21.47) * mm});
            skSolve(sketch);
        }
        {
            var Q0;
            Q0 = qSketchRegion(id + "F16", true);
            extrude(context, id + "F17", {"entities" : qUnion([Q0]), "operationType" : NewBodyOperationType.ADD, "depth" : 6 * mm});
        }
        {
            var Q0;
            Q0=makeQuery(id+"F15.opExtrude","CAP_FACE",FACE,{"disambiguationData":[OSD([sQuery(id+"F14.wireOp",EDGE,"E80.bottom"),sQuery(id+"F14.wireOp",EDGE,"E80.top"),sQuery(id+"F14.wireOp",EDGE,"E80.left"),sQuery(id+"F14.wireOp",EDGE,"E80.right")])],"isStart":false});
            var sketch = newSketch(context, id + "F18", { "sketchPlane" : qUnion([Q0])});
            skCircle(sketch, "E83", {"center": v(-4.68, -24.47) * mm, "radius": 3 * mm});
            skPoint(sketch, "E83.centerSnap0", {"position": v(-1.68, -24.47) * mm});
            skPoint(sketch, "E83.centerSnap1", {"position": v(-4.68, -21.47) * mm});
            skSolve(sketch);
        }
        {
            var Q0;
            Q0 = qSketchRegion(id + "F18", true);
            extrude(context, id + "F19", {"entities" : qUnion([Q0]), "operationType" : NewBodyOperationType.ADD, "depth" : 6 * mm});
        }
    });
